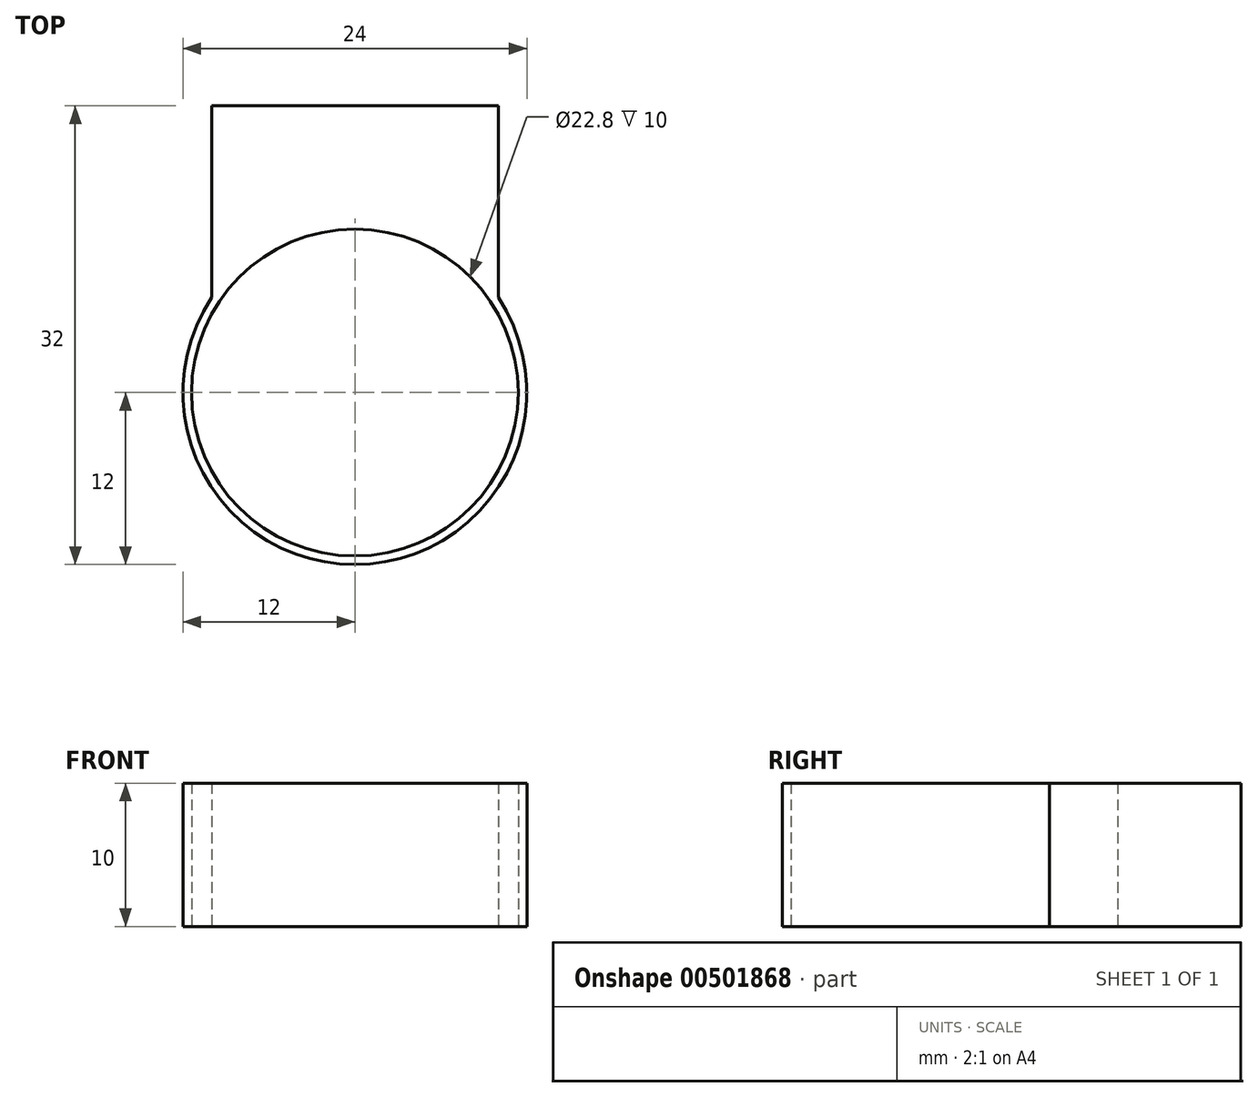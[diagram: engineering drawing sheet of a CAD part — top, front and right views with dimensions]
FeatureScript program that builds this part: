
annotation { "Feature Type Name" : "Feature", "Feature Type Description" : "" }
export const myFeature = defineFeature(function(context is Context, id is Id, definition is map)
    precondition{}
    {
        {
            var Q0;
            Q0=qCreatedBy(makeId("Top.planeOp"),FACE);
            var sketch = newSketch(context, id + "F0", { "sketchPlane" : qUnion([Q0])});
            skCircle(sketch, "E0", {"center": v(0, 0) * mm, "radius": 11.4 * mm});
            skCircle(sketch, "E1", {"center": v(0, 0) * mm, "radius": 12 * mm});
            skLineSegment(sketch, "E2.bottom", {"start": v(-10, 20) * mm, "end": v(10, 20) * mm});
            skLineSegment(sketch, "E2.left", {"start": v(-10, 20) * mm, "end": v(-10, 0) * mm});
            skLineSegment(sketch, "E2.right", {"start": v(10, 20) * mm, "end": v(10, 0) * mm});
            skPoint(sketch, "E2.middle", {"position": v(0, 10) * mm});
            skSolve(sketch);
        }
        {
            var Q0;
            Q0 = qSketchRegion(id + "F0", true);
            extrude(context, id + "F1", {"entities" : qUnion([Q0]), "depth" : 10 * mm});
        }
    });
